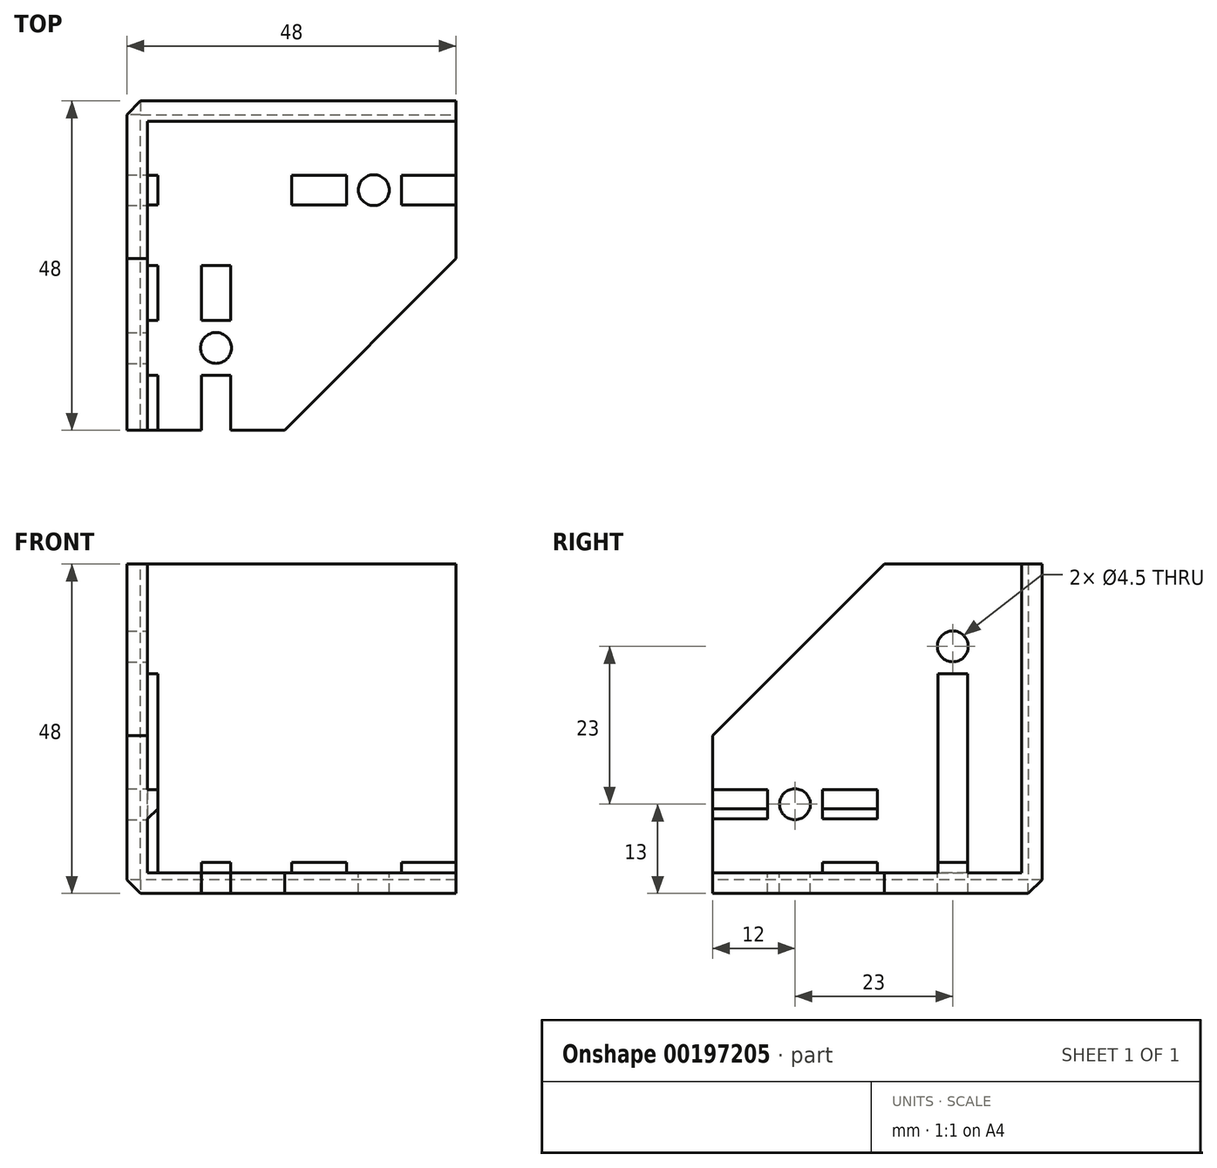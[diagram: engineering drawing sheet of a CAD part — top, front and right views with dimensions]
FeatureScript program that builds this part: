
annotation { "Feature Type Name" : "Feature", "Feature Type Description" : "" }
export const myFeature = defineFeature(function(context is Context, id is Id, definition is map)
    precondition{}
    {
        {
            var Q0;
            Q0=qCreatedBy(makeId("Top.planeOp"),FACE);
            var sketch = newSketch(context, id + "F0", { "sketchPlane" : qUnion([Q0])});
            skLineSegment(sketch, "E0", {"start": v(0, 0) * mm, "end": v(0, -45) * mm});
            skLineSegment(sketch, "E1", {"start": v(0, -45) * mm, "end": v(20, -45) * mm});
            skLineSegment(sketch, "E2", {"start": v(20, -45) * mm, "end": v(45, -20) * mm});
            skLineSegment(sketch, "E3", {"start": v(45, -20) * mm, "end": v(45, 0) * mm});
            skLineSegment(sketch, "E4", {"start": v(45, 0) * mm, "end": v(0, 0) * mm});
            skLineSegment(sketch, "E5", {"start": v(45, 0) * mm, "end": v(45, 3) * mm});
            skLineSegment(sketch, "E6", {"start": v(45, 3) * mm, "end": v(-3, 3) * mm});
            skLineSegment(sketch, "E7", {"start": v(-3, 3) * mm, "end": v(-3, -45) * mm});
            skLineSegment(sketch, "E8", {"start": v(-3, -45) * mm, "end": v(0, -45) * mm});
            skCircle(sketch, "E9", {"center": v(33, -10) * mm, "radius": 2.25 * mm});
            skPoint(sketch, "E9.centerSnap0", {"position": v(45, -10) * mm});
            skCircle(sketch, "E10", {"center": v(10, -33) * mm, "radius": 2.25 * mm});
            skPoint(sketch, "E10.centerSnap0", {"position": v(10, -45) * mm});
            skLineSegment(sketch, "E11.bottom", {"start": v(29, -12.15) * mm, "end": v(21, -12.15) * mm});
            skLineSegment(sketch, "E11.top", {"start": v(29, -7.85) * mm, "end": v(21, -7.85) * mm});
            skLineSegment(sketch, "E11.left", {"start": v(29, -12.15) * mm, "end": v(29, -7.85) * mm});
            skLineSegment(sketch, "E11.right", {"start": v(21, -12.15) * mm, "end": v(21, -7.85) * mm});
            skPoint(sketch, "E11.middle", {"position": v(25, -10) * mm});
            skLineSegment(sketch, "E12.bottom", {"start": v(45, -7.85) * mm, "end": v(37, -7.85) * mm});
            skLineSegment(sketch, "E12.top", {"start": v(45, -12.15) * mm, "end": v(37, -12.15) * mm});
            skLineSegment(sketch, "E12.left", {"start": v(45, -7.85) * mm, "end": v(45, -12.15) * mm});
            skLineSegment(sketch, "E12.right", {"start": v(37, -7.85) * mm, "end": v(37, -12.15) * mm});
            skPoint(sketch, "E12.middle", {"position": v(41, -10) * mm});
            skLineSegment(sketch, "E13.bottom", {"start": v(12.15, -29) * mm, "end": v(7.85, -29) * mm});
            skLineSegment(sketch, "E13.top", {"start": v(12.15, -21) * mm, "end": v(7.85, -21) * mm});
            skLineSegment(sketch, "E13.left", {"start": v(12.15, -29) * mm, "end": v(12.15, -21) * mm});
            skLineSegment(sketch, "E13.right", {"start": v(7.85, -29) * mm, "end": v(7.85, -21) * mm});
            skPoint(sketch, "E13.middle", {"position": v(10, -25) * mm});
            skLineSegment(sketch, "E14.bottom", {"start": v(12.15, -45) * mm, "end": v(7.85, -45) * mm});
            skLineSegment(sketch, "E14.top", {"start": v(12.15, -37) * mm, "end": v(7.85, -37) * mm});
            skLineSegment(sketch, "E14.left", {"start": v(12.15, -45) * mm, "end": v(12.15, -37) * mm});
            skLineSegment(sketch, "E14.right", {"start": v(7.85, -45) * mm, "end": v(7.85, -37) * mm});
            skPoint(sketch, "E14.middle", {"position": v(10, -41) * mm});
            skSolve(sketch);
        }
        {
            var Q0;
            Q0=makeQuery(id+"F0.imprint","IMPRINT",FACE,{"disambiguationData":[TD([[makeQuery(id+"F0.imprint","IMPRINT",EDGE,{"derivedFrom":sQuery(id+"F0.wireOp",EDGE,"E0")}),-1.0]])]});
            var Q1;
            {var subQ5=sQuery(id+"F0.wireOp",EDGE,"E0");Q1=makeQuery(id+"F0.imprint","IMPRINT",FACE,{"disambiguationData":[TD([[makeQuery(id+"F0.imprint","IMPRINT",EDGE,{"derivedFrom":subQ5}),1.0]])]});}
            var Q2;
            Q2=makeQuery(id+"F0.imprint","IMPRINT",FACE,{"disambiguationData":[TD([[makeQuery(id+"F0.imprint","IMPRINT",EDGE,{"derivedFrom":sQuery(id+"F0.wireOp",EDGE,"E11.bottom")}),-1.0]])]});
            var Q3;
            Q3=makeQuery(id+"F0.imprint","IMPRINT",FACE,{"disambiguationData":[TD([[makeQuery(id+"F0.imprint","IMPRINT",EDGE,{"derivedFrom":sQuery(id+"F0.wireOp",EDGE,"E12.bottom")}),1.0]])]});
            var Q4;
            Q4=makeQuery(id+"F0.imprint","IMPRINT",FACE,{"disambiguationData":[TD([[makeQuery(id+"F0.imprint","IMPRINT",EDGE,{"derivedFrom":sQuery(id+"F0.wireOp",EDGE,"E13.bottom")}),-1.0]])]});
            var Q5;
            Q5=makeQuery(id+"F0.imprint","IMPRINT",FACE,{"disambiguationData":[TD([[makeQuery(id+"F0.imprint","IMPRINT",EDGE,{"derivedFrom":sQuery(id+"F0.wireOp",EDGE,"E14.bottom")}),-1.0]])]});
            extrude(context, id + "F1", {"entities" : qUnion([Q0, Q1, Q2, Q3, Q4, Q5]), "oppositeDirection" : true, "depth" : 3 * mm});
        }
        {
            var Q0;
            Q0=makeQuery(id+"F0.imprint","IMPRINT",FACE,{"disambiguationData":[TD([[makeQuery(id+"F0.imprint","IMPRINT",EDGE,{"derivedFrom":sQuery(id+"F0.wireOp",EDGE,"E0")}),-1.0]])]});
            extrude(context, id + "F2", {"entities" : qUnion([Q0]), "operationType" : NewBodyOperationType.ADD, "depth" : 45 * mm});
        }
        {
            var Q0;
            Q0=makeQuery(id+"F0.imprint","IMPRINT",FACE,{"disambiguationData":[TD([[makeQuery(id+"F0.imprint","IMPRINT",EDGE,{"derivedFrom":sQuery(id+"F0.wireOp",EDGE,"E13.bottom")}),-1.0]])]});
            var Q1;
            Q1=makeQuery(id+"F0.imprint","IMPRINT",FACE,{"disambiguationData":[TD([[makeQuery(id+"F0.imprint","IMPRINT",EDGE,{"derivedFrom":sQuery(id+"F0.wireOp",EDGE,"E14.bottom")}),-1.0]])]});
            var Q2;
            Q2=makeQuery(id+"F0.imprint","IMPRINT",FACE,{"disambiguationData":[TD([[makeQuery(id+"F0.imprint","IMPRINT",EDGE,{"derivedFrom":sQuery(id+"F0.wireOp",EDGE,"E11.bottom")}),-1.0]])]});
            var Q3;
            Q3=makeQuery(id+"F0.imprint","IMPRINT",FACE,{"disambiguationData":[TD([[makeQuery(id+"F0.imprint","IMPRINT",EDGE,{"derivedFrom":sQuery(id+"F0.wireOp",EDGE,"E12.bottom")}),1.0]])]});
            extrude(context, id + "F3", {"entities" : qUnion([Q0, Q1, Q2, Q3]), "operationType" : NewBodyOperationType.ADD, "depth" : 1.5 * mm});
        }
        {
            var Q0;
            Q0=makeQuery(id+"F2.opExtrude","SWEPT_FACE",FACE,{"disambiguationData":[OSD([sQuery(id+"F0.wireOp",EDGE,"E0")])]});
            var sketch = newSketch(context, id + "F4", { "sketchPlane" : qUnion([Q0])});
            skLineSegment(sketch, "E15", {"start": v(-20, 45) * mm, "end": v(-45, 20) * mm});
            skLineSegment(sketch, "E16", {"start": v(0, 45) * mm, "end": v(-20, 45) * mm});
            skLineSegment(sketch, "E17", {"start": v(-45, 20) * mm, "end": v(-45, 0) * mm});
            skCircle(sketch, "E18", {"center": v(-10, 33) * mm, "radius": 2.25 * mm});
            skPoint(sketch, "E18.centerSnap0", {"position": v(-10, 45) * mm});
            skCircle(sketch, "E19", {"center": v(-33, 10) * mm, "radius": 2.25 * mm});
            skPoint(sketch, "E19.centerSnap0", {"position": v(-45, 10) * mm});
            skLineSegment(sketch, "E20.bottom", {"start": v(-45, 12.15) * mm, "end": v(-37, 12.15) * mm});
            skLineSegment(sketch, "E20.top", {"start": v(-45, 7.85) * mm, "end": v(-37, 7.85) * mm});
            skLineSegment(sketch, "E20.left", {"start": v(-45, 12.15) * mm, "end": v(-45, 7.85) * mm});
            skLineSegment(sketch, "E20.right", {"start": v(-37, 12.15) * mm, "end": v(-37, 7.85) * mm});
            skPoint(sketch, "E20.middle", {"position": v(-41, 10) * mm});
            skLineSegment(sketch, "E21.bottom", {"start": v(-29, 12.15) * mm, "end": v(-21, 12.15) * mm});
            skLineSegment(sketch, "E21.top", {"start": v(-29, 7.85) * mm, "end": v(-21, 7.85) * mm});
            skLineSegment(sketch, "E21.left", {"start": v(-29, 12.15) * mm, "end": v(-29, 7.85) * mm});
            skLineSegment(sketch, "E21.right", {"start": v(-21, 12.15) * mm, "end": v(-21, 7.85) * mm});
            skPoint(sketch, "E21.middle", {"position": v(-25, 10) * mm});
            skLineSegment(sketch, "E22.bottom", {"start": v(-7.85, 45) * mm, "end": v(-12.15, 45) * mm});
            skLineSegment(sketch, "E22.top", {"start": v(-7.85, 37) * mm, "end": v(-12.15, 37) * mm});
            skLineSegment(sketch, "E22.left", {"start": v(-7.85, 45) * mm, "end": v(-7.85, 37) * mm});
            skLineSegment(sketch, "E22.right", {"start": v(-12.15, 45) * mm, "end": v(-12.15, 37) * mm});
            skPoint(sketch, "E22.middle", {"position": v(-10, 41) * mm});
            skLineSegment(sketch, "E23.bottom", {"start": v(-7.85, 29) * mm, "end": v(-12.15, 29) * mm});
            skLineSegment(sketch, "E23.top", {"start": v(-7.85, 21) * mm, "end": v(-12.15, 21) * mm});
            skLineSegment(sketch, "E23.left", {"start": v(-7.85, 29) * mm, "end": v(-7.85, 21) * mm});
            skLineSegment(sketch, "E23.right", {"start": v(-12.15, 29) * mm, "end": v(-12.15, 21) * mm});
            skPoint(sketch, "E23.middle", {"position": v(-10, 25) * mm});
            skLineSegment(sketch, "E24", {"start": v(-12.15, 21) * mm, "end": v(-12.15, 0) * mm});
            skLineSegment(sketch, "E25", {"start": v(-7.85, 21) * mm, "end": v(-7.85, 0) * mm});
            skSolve(sketch);
        }
        {
            var Q0;
            {var subQ0=sQuery(id+"F4.wireOp",EDGE,"E15");Q0=makeQuery(id+"F4.imprint","IMPRINT",FACE,{"disambiguationData":[TD([[makeQuery(id+"F4.imprint","IMPRINT",EDGE,{"derivedFrom":subQ0}),-1.0]])]});}
            var Q1;
            Q1=makeQuery(id+"F4.imprint","IMPRINT",FACE,{"disambiguationData":[TD([[makeQuery(id+"F4.imprint","IMPRINT",EDGE,{"derivedFrom":sQuery(id+"F4.wireOp",EDGE,"E18")}),1.0]])]});
            var Q2;
            Q2=makeQuery(id+"F4.imprint","IMPRINT",FACE,{"disambiguationData":[TD([[makeQuery(id+"F4.imprint","IMPRINT",EDGE,{"derivedFrom":sQuery(id+"F4.wireOp",EDGE,"E19")}),1.0]])]});
            extrude(context, id + "F5", {"entities" : qUnion([Q0, Q1, Q2]), "operationType" : NewBodyOperationType.REMOVE, "oppositeDirection" : true, "depth" : 25 * mm, "symmetric" : true});
        }
        {
            var Q0;
            Q0=makeQuery(id+"F4.imprint","IMPRINT",FACE,{"disambiguationData":[TD([[makeQuery(id+"F4.imprint","IMPRINT",EDGE,{"derivedFrom":sQuery(id+"F4.wireOp",EDGE,"E22.bottom")}),1.0]])]});
            var Q1;
            Q1=makeQuery(id+"F4.imprint","IMPRINT",FACE,{"disambiguationData":[TD([[makeQuery(id+"F4.imprint","IMPRINT",EDGE,{"derivedFrom":sQuery(id+"F4.wireOp",EDGE,"E23.bottom")}),1.0]])]});
            var Q2;
            Q2=makeQuery(id+"F4.imprint","IMPRINT",FACE,{"disambiguationData":[TD([[makeQuery(id+"F4.imprint","IMPRINT",EDGE,{"derivedFrom":sQuery(id+"F4.wireOp",EDGE,"E23.top")}),1.0]])]});
            var Q3;
            Q3=makeQuery(id+"F4.imprint","IMPRINT",FACE,{"disambiguationData":[TD([[makeQuery(id+"F4.imprint","IMPRINT",EDGE,{"derivedFrom":sQuery(id+"F4.wireOp",EDGE,"E21.bottom")}),-1.0]])]});
            var Q4;
            Q4=makeQuery(id+"F4.imprint","IMPRINT",FACE,{"disambiguationData":[TD([[makeQuery(id+"F4.imprint","IMPRINT",EDGE,{"derivedFrom":sQuery(id+"F4.wireOp",EDGE,"E20.bottom")}),-1.0]])]});
            extrude(context, id + "F6", {"entities" : qUnion([Q0, Q1, Q2, Q3, Q4]), "operationType" : NewBodyOperationType.ADD, "depth" : 1.5 * mm});
        }
        {
            var Q0;
            Q0=makeQuery(id+"F6.opExtrude","CAP_EDGE",EDGE,{"disambiguationData":[OSD([sQuery(id+"F4.wireOp",EDGE,"E20.top")])],"isStart":false});
            var Q1;
            Q1=makeQuery(id+"F6.opExtrude","CAP_EDGE",EDGE,{"disambiguationData":[OSD([sQuery(id+"F4.wireOp",EDGE,"E21.top")])],"isStart":false});
            var Q2;
            Q2=makeQuery(id+"F6.opExtrude","CAP_EDGE",EDGE,{"disambiguationData":[OSD([sQuery(id+"F4.wireOp",EDGE,"E22.top")])],"isStart":false});
            chamfer(context, id + "F7", {"entities" : qUnion([Q0, Q1, Q2]), "width" : 1.5 * mm, "tangentPropagation" : true});
        }
        {
            var Q0;
            Q0=qCreatedBy(makeId("Front.planeOp"),FACE);
            var Q1;
            Q1=qCreatedBy(makeId("Right.planeOp"),FACE);
            cPlane(context, id + "F8", {"entities" : qUnion([Q0, Q1]), "cplaneType" : CPlaneType.MID_PLANE, "offset" : 25 * mm, "width" : 150 * mm, "height" : 150 * mm});
        }
        {
            var Q0;
            {var subQ0=sQuery(id+"F0.wireOp",EDGE,"E7");var subQ1=sQuery(id+"F0.wireOp",EDGE,"E6");Q0=makeQuery(id+"F2.boolean.opBoolean","MERGE",EDGE,{"derivedFrom":[makeQuery(id+"F1.opExtrude","SWEPT_EDGE",EDGE,{"disambiguationData":[OSD([subQ1,subQ0])]}),makeQuery(id+"F2.opExtrude","SWEPT_EDGE",EDGE,{"disambiguationData":[OSD([subQ1,subQ0])]})]});}
            var Q1;
            Q1=makeQuery(id+"F1.opExtrude","CAP_EDGE",EDGE,{"disambiguationData":[OSD([sQuery(id+"F0.wireOp",EDGE,"E7")])],"isStart":false});
            var Q2;
            Q2=makeQuery(id+"F1.opExtrude","CAP_EDGE",EDGE,{"disambiguationData":[OSD([sQuery(id+"F0.wireOp",EDGE,"E6")])],"isStart":false});
            chamfer(context, id + "F9", {"entities" : qUnion([Q0, Q1, Q2]), "width" : 2 * mm, "tangentPropagation" : true});
        }
    });
